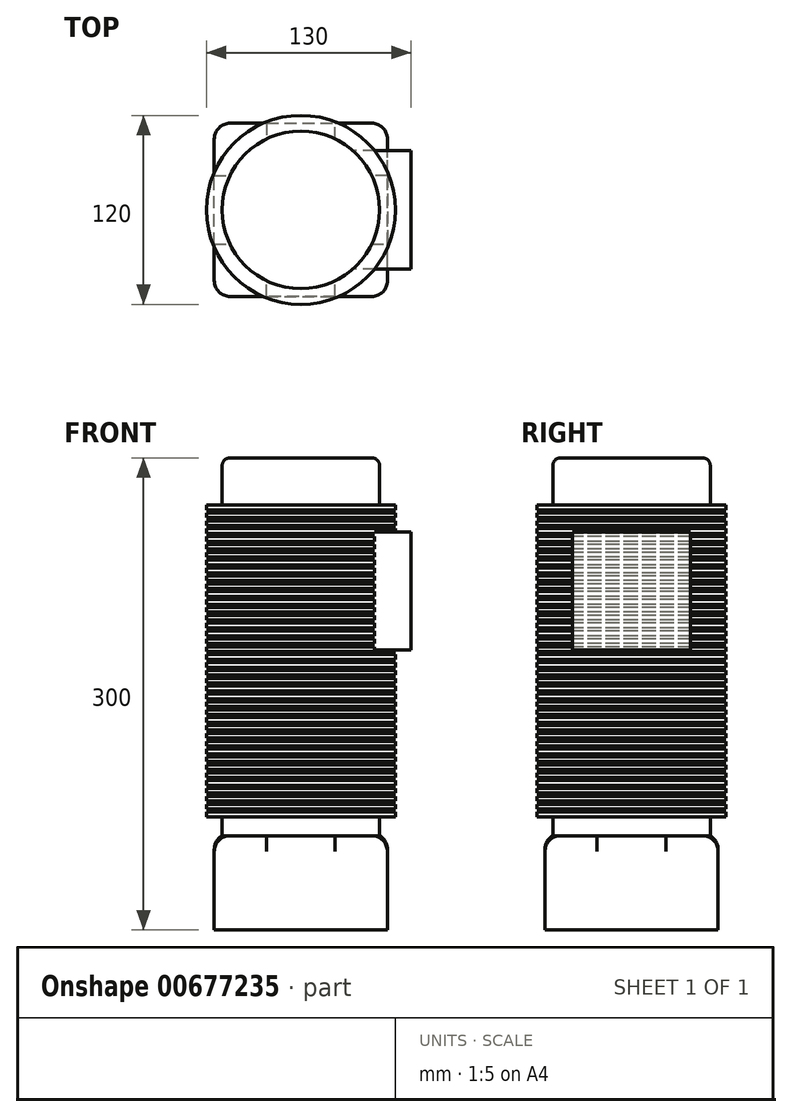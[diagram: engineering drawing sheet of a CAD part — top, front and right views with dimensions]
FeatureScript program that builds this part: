
annotation { "Feature Type Name" : "Feature", "Feature Type Description" : "" }
export const myFeature = defineFeature(function(context is Context, id is Id, definition is map)
    precondition{}
    {
        {
            var Q0;
            Q0=qCreatedBy(makeId("Front.planeOp"),FACE);
            var sketch = newSketch(context, id + "F0", { "sketchPlane" : qUnion([Q0])});
            skLineSegment(sketch, "E0.bottom", {"start": v(0, 0) * mm, "end": v(50, 0) * mm});
            skLineSegment(sketch, "E0.top", {"start": v(0, 300) * mm, "end": v(50, 300) * mm});
            skLineSegment(sketch, "E0.left", {"start": v(0, 0) * mm, "end": v(0, 300) * mm});
            skLineSegment(sketch, "E0.right", {"start": v(50, 0) * mm, "end": v(50, 300) * mm});
            skSolve(sketch);
        }
        {
            var Q0;
            Q0=makeQuery(id+"F0.imprint","IMPRINT",FACE,{"disambiguationData":[TD([[makeQuery(id+"F0.imprint","IMPRINT",EDGE,{"derivedFrom":sQuery(id+"F0.wireOp",EDGE,"E0.bottom")}),1.0]])]});
            var Q1;
            Q1=sQuery(id+"F0.wireOp",EDGE,"E0.left");
            revolve(context, id + "F1", {"entities" : qUnion([Q0]), "axis" : qUnion([Q1]), "revolveType" : RevolveType.FULL});
        }
        {
            var Q0;
            Q0=qCreatedBy(makeId("Front.planeOp"),FACE);
            var sketch = newSketch(context, id + "F2", { "sketchPlane" : qUnion([Q0])});
            skLineSegment(sketch, "E1", {"start": v(50, 300) * mm, "end": v(50, 0) * mm});
            skLineSegment(sketch, "E2.bottom", {"start": v(50, 270) * mm, "end": v(60, 270) * mm});
            skLineSegment(sketch, "E2.top", {"start": v(50, 267) * mm, "end": v(60, 267) * mm});
            skLineSegment(sketch, "E2.left", {"start": v(50, 270) * mm, "end": v(50, 267) * mm});
            skLineSegment(sketch, "E2.right", {"start": v(60, 270) * mm, "end": v(60, 267) * mm});
            skLineSegment(sketch, "E3.0.1.0", {"start": v(50, 265) * mm, "end": v(60, 265) * mm});
            skLineSegment(sketch, "E3.0.1.1", {"start": v(50, 262) * mm, "end": v(60, 262) * mm});
            skLineSegment(sketch, "E3.0.1.2", {"start": v(50, 265) * mm, "end": v(50, 262) * mm});
            skLineSegment(sketch, "E3.0.1.3", {"start": v(60, 265) * mm, "end": v(60, 262) * mm});
            skLineSegment(sketch, "E3.0.2.0", {"start": v(50, 260) * mm, "end": v(60, 260) * mm});
            skLineSegment(sketch, "E3.0.2.1", {"start": v(50, 257) * mm, "end": v(60, 257) * mm});
            skLineSegment(sketch, "E3.0.2.2", {"start": v(50, 260) * mm, "end": v(50, 257) * mm});
            skLineSegment(sketch, "E3.0.2.3", {"start": v(60, 260) * mm, "end": v(60, 257) * mm});
            skLineSegment(sketch, "E3.0.3.0", {"start": v(50, 255) * mm, "end": v(60, 255) * mm});
            skLineSegment(sketch, "E3.0.3.1", {"start": v(50, 252) * mm, "end": v(60, 252) * mm});
            skLineSegment(sketch, "E3.0.3.2", {"start": v(50, 255) * mm, "end": v(50, 252) * mm});
            skLineSegment(sketch, "E3.0.3.3", {"start": v(60, 255) * mm, "end": v(60, 252) * mm});
            skLineSegment(sketch, "E3.0.4.0", {"start": v(50, 250) * mm, "end": v(60, 250) * mm});
            skLineSegment(sketch, "E3.0.4.1", {"start": v(50, 247) * mm, "end": v(60, 247) * mm});
            skLineSegment(sketch, "E3.0.4.2", {"start": v(50, 250) * mm, "end": v(50, 247) * mm});
            skLineSegment(sketch, "E3.0.4.3", {"start": v(60, 250) * mm, "end": v(60, 247) * mm});
            skLineSegment(sketch, "E3.0.5.0", {"start": v(50, 245) * mm, "end": v(60, 245) * mm});
            skLineSegment(sketch, "E3.0.5.1", {"start": v(50, 242) * mm, "end": v(60, 242) * mm});
            skLineSegment(sketch, "E3.0.5.2", {"start": v(50, 245) * mm, "end": v(50, 242) * mm});
            skLineSegment(sketch, "E3.0.5.3", {"start": v(60, 245) * mm, "end": v(60, 242) * mm});
            skLineSegment(sketch, "E3.0.6.0", {"start": v(50, 240) * mm, "end": v(60, 240) * mm});
            skLineSegment(sketch, "E3.0.6.1", {"start": v(50, 237) * mm, "end": v(60, 237) * mm});
            skLineSegment(sketch, "E3.0.6.2", {"start": v(50, 240) * mm, "end": v(50, 237) * mm});
            skLineSegment(sketch, "E3.0.6.3", {"start": v(60, 240) * mm, "end": v(60, 237) * mm});
            skLineSegment(sketch, "E3.0.7.0", {"start": v(50, 235) * mm, "end": v(60, 235) * mm});
            skLineSegment(sketch, "E3.0.7.1", {"start": v(50, 232) * mm, "end": v(60, 232) * mm});
            skLineSegment(sketch, "E3.0.7.2", {"start": v(50, 235) * mm, "end": v(50, 232) * mm});
            skLineSegment(sketch, "E3.0.7.3", {"start": v(60, 235) * mm, "end": v(60, 232) * mm});
            skLineSegment(sketch, "E3.0.8.0", {"start": v(50, 230) * mm, "end": v(60, 230) * mm});
            skLineSegment(sketch, "E3.0.8.1", {"start": v(50, 227) * mm, "end": v(60, 227) * mm});
            skLineSegment(sketch, "E3.0.8.2", {"start": v(50, 230) * mm, "end": v(50, 227) * mm});
            skLineSegment(sketch, "E3.0.8.3", {"start": v(60, 230) * mm, "end": v(60, 227) * mm});
            skLineSegment(sketch, "E3.0.9.0", {"start": v(50, 225) * mm, "end": v(60, 225) * mm});
            skLineSegment(sketch, "E3.0.9.1", {"start": v(50, 222) * mm, "end": v(60, 222) * mm});
            skLineSegment(sketch, "E3.0.9.2", {"start": v(50, 225) * mm, "end": v(50, 222) * mm});
            skLineSegment(sketch, "E3.0.9.3", {"start": v(60, 225) * mm, "end": v(60, 222) * mm});
            skLineSegment(sketch, "E3.0.10.0", {"start": v(50, 220) * mm, "end": v(60, 220) * mm});
            skLineSegment(sketch, "E3.0.10.1", {"start": v(50, 217) * mm, "end": v(60, 217) * mm});
            skLineSegment(sketch, "E3.0.10.2", {"start": v(50, 220) * mm, "end": v(50, 217) * mm});
            skLineSegment(sketch, "E3.0.10.3", {"start": v(60, 220) * mm, "end": v(60, 217) * mm});
            skLineSegment(sketch, "E3.0.11.0", {"start": v(50, 215) * mm, "end": v(60, 215) * mm});
            skLineSegment(sketch, "E3.0.11.1", {"start": v(50, 212) * mm, "end": v(60, 212) * mm});
            skLineSegment(sketch, "E3.0.11.2", {"start": v(50, 215) * mm, "end": v(50, 212) * mm});
            skLineSegment(sketch, "E3.0.11.3", {"start": v(60, 215) * mm, "end": v(60, 212) * mm});
            skLineSegment(sketch, "E3.0.12.0", {"start": v(50, 210) * mm, "end": v(60, 210) * mm});
            skLineSegment(sketch, "E3.0.12.1", {"start": v(50, 207) * mm, "end": v(60, 207) * mm});
            skLineSegment(sketch, "E3.0.12.2", {"start": v(50, 210) * mm, "end": v(50, 207) * mm});
            skLineSegment(sketch, "E3.0.12.3", {"start": v(60, 210) * mm, "end": v(60, 207) * mm});
            skLineSegment(sketch, "E3.0.13.0", {"start": v(50, 205) * mm, "end": v(60, 205) * mm});
            skLineSegment(sketch, "E3.0.13.1", {"start": v(50, 202) * mm, "end": v(60, 202) * mm});
            skLineSegment(sketch, "E3.0.13.2", {"start": v(50, 205) * mm, "end": v(50, 202) * mm});
            skLineSegment(sketch, "E3.0.13.3", {"start": v(60, 205) * mm, "end": v(60, 202) * mm});
            skLineSegment(sketch, "E3.0.14.0", {"start": v(50, 200) * mm, "end": v(60, 200) * mm});
            skLineSegment(sketch, "E3.0.14.1", {"start": v(50, 197) * mm, "end": v(60, 197) * mm});
            skLineSegment(sketch, "E3.0.14.2", {"start": v(50, 200) * mm, "end": v(50, 197) * mm});
            skLineSegment(sketch, "E3.0.14.3", {"start": v(60, 200) * mm, "end": v(60, 197) * mm});
            skLineSegment(sketch, "E3.0.15.0", {"start": v(50, 195) * mm, "end": v(60, 195) * mm});
            skLineSegment(sketch, "E3.0.15.1", {"start": v(50, 192) * mm, "end": v(60, 192) * mm});
            skLineSegment(sketch, "E3.0.15.2", {"start": v(50, 195) * mm, "end": v(50, 192) * mm});
            skLineSegment(sketch, "E3.0.15.3", {"start": v(60, 195) * mm, "end": v(60, 192) * mm});
            skLineSegment(sketch, "E3.0.16.0", {"start": v(50, 190) * mm, "end": v(60, 190) * mm});
            skLineSegment(sketch, "E3.0.16.1", {"start": v(50, 187) * mm, "end": v(60, 187) * mm});
            skLineSegment(sketch, "E3.0.16.2", {"start": v(50, 190) * mm, "end": v(50, 187) * mm});
            skLineSegment(sketch, "E3.0.16.3", {"start": v(60, 190) * mm, "end": v(60, 187) * mm});
            skLineSegment(sketch, "E3.0.17.0", {"start": v(50, 185) * mm, "end": v(60, 185) * mm});
            skLineSegment(sketch, "E3.0.17.1", {"start": v(50, 182) * mm, "end": v(60, 182) * mm});
            skLineSegment(sketch, "E3.0.17.2", {"start": v(50, 185) * mm, "end": v(50, 182) * mm});
            skLineSegment(sketch, "E3.0.17.3", {"start": v(60, 185) * mm, "end": v(60, 182) * mm});
            skLineSegment(sketch, "E3.0.18.0", {"start": v(50, 180) * mm, "end": v(60, 180) * mm});
            skLineSegment(sketch, "E3.0.18.1", {"start": v(50, 177) * mm, "end": v(60, 177) * mm});
            skLineSegment(sketch, "E3.0.18.2", {"start": v(50, 180) * mm, "end": v(50, 177) * mm});
            skLineSegment(sketch, "E3.0.18.3", {"start": v(60, 180) * mm, "end": v(60, 177) * mm});
            skLineSegment(sketch, "E3.0.19.0", {"start": v(50, 175) * mm, "end": v(60, 175) * mm});
            skLineSegment(sketch, "E3.0.19.1", {"start": v(50, 172) * mm, "end": v(60, 172) * mm});
            skLineSegment(sketch, "E3.0.19.2", {"start": v(50, 175) * mm, "end": v(50, 172) * mm});
            skLineSegment(sketch, "E3.0.19.3", {"start": v(60, 175) * mm, "end": v(60, 172) * mm});
            skLineSegment(sketch, "E3.0.20.0", {"start": v(50, 170) * mm, "end": v(60, 170) * mm});
            skLineSegment(sketch, "E3.0.20.1", {"start": v(50, 167) * mm, "end": v(60, 167) * mm});
            skLineSegment(sketch, "E3.0.20.2", {"start": v(50, 170) * mm, "end": v(50, 167) * mm});
            skLineSegment(sketch, "E3.0.20.3", {"start": v(60, 170) * mm, "end": v(60, 167) * mm});
            skLineSegment(sketch, "E3.0.21.0", {"start": v(50, 165) * mm, "end": v(60, 165) * mm});
            skLineSegment(sketch, "E3.0.21.1", {"start": v(50, 162) * mm, "end": v(60, 162) * mm});
            skLineSegment(sketch, "E3.0.21.2", {"start": v(50, 165) * mm, "end": v(50, 162) * mm});
            skLineSegment(sketch, "E3.0.21.3", {"start": v(60, 165) * mm, "end": v(60, 162) * mm});
            skLineSegment(sketch, "E3.0.22.0", {"start": v(50, 160) * mm, "end": v(60, 160) * mm});
            skLineSegment(sketch, "E3.0.22.1", {"start": v(50, 157) * mm, "end": v(60, 157) * mm});
            skLineSegment(sketch, "E3.0.22.2", {"start": v(50, 160) * mm, "end": v(50, 157) * mm});
            skLineSegment(sketch, "E3.0.22.3", {"start": v(60, 160) * mm, "end": v(60, 157) * mm});
            skLineSegment(sketch, "E3.0.23.0", {"start": v(50, 155) * mm, "end": v(60, 155) * mm});
            skLineSegment(sketch, "E3.0.23.1", {"start": v(50, 152) * mm, "end": v(60, 152) * mm});
            skLineSegment(sketch, "E3.0.23.2", {"start": v(50, 155) * mm, "end": v(50, 152) * mm});
            skLineSegment(sketch, "E3.0.23.3", {"start": v(60, 155) * mm, "end": v(60, 152) * mm});
            skLineSegment(sketch, "E3.0.24.0", {"start": v(50, 150) * mm, "end": v(60, 150) * mm});
            skLineSegment(sketch, "E3.0.24.1", {"start": v(50, 147) * mm, "end": v(60, 147) * mm});
            skLineSegment(sketch, "E3.0.24.2", {"start": v(50, 150) * mm, "end": v(50, 147) * mm});
            skLineSegment(sketch, "E3.0.24.3", {"start": v(60, 150) * mm, "end": v(60, 147) * mm});
            skLineSegment(sketch, "E3.0.25.0", {"start": v(50, 145) * mm, "end": v(60, 145) * mm});
            skLineSegment(sketch, "E3.0.25.1", {"start": v(50, 142) * mm, "end": v(60, 142) * mm});
            skLineSegment(sketch, "E3.0.25.2", {"start": v(50, 145) * mm, "end": v(50, 142) * mm});
            skLineSegment(sketch, "E3.0.25.3", {"start": v(60, 145) * mm, "end": v(60, 142) * mm});
            skLineSegment(sketch, "E3.0.26.0", {"start": v(50, 140) * mm, "end": v(60, 140) * mm});
            skLineSegment(sketch, "E3.0.26.1", {"start": v(50, 137) * mm, "end": v(60, 137) * mm});
            skLineSegment(sketch, "E3.0.26.2", {"start": v(50, 140) * mm, "end": v(50, 137) * mm});
            skLineSegment(sketch, "E3.0.26.3", {"start": v(60, 140) * mm, "end": v(60, 137) * mm});
            skLineSegment(sketch, "E3.0.27.0", {"start": v(50, 135) * mm, "end": v(60, 135) * mm});
            skLineSegment(sketch, "E3.0.27.1", {"start": v(50, 132) * mm, "end": v(60, 132) * mm});
            skLineSegment(sketch, "E3.0.27.2", {"start": v(50, 135) * mm, "end": v(50, 132) * mm});
            skLineSegment(sketch, "E3.0.27.3", {"start": v(60, 135) * mm, "end": v(60, 132) * mm});
            skLineSegment(sketch, "E3.0.28.0", {"start": v(50, 130) * mm, "end": v(60, 130) * mm});
            skLineSegment(sketch, "E3.0.28.1", {"start": v(50, 127) * mm, "end": v(60, 127) * mm});
            skLineSegment(sketch, "E3.0.28.2", {"start": v(50, 130) * mm, "end": v(50, 127) * mm});
            skLineSegment(sketch, "E3.0.28.3", {"start": v(60, 130) * mm, "end": v(60, 127) * mm});
            skLineSegment(sketch, "E3.0.29.0", {"start": v(50, 125) * mm, "end": v(60, 125) * mm});
            skLineSegment(sketch, "E3.0.29.1", {"start": v(50, 122) * mm, "end": v(60, 122) * mm});
            skLineSegment(sketch, "E3.0.29.2", {"start": v(50, 125) * mm, "end": v(50, 122) * mm});
            skLineSegment(sketch, "E3.0.29.3", {"start": v(60, 125) * mm, "end": v(60, 122) * mm});
            skLineSegment(sketch, "E3.0.30.0", {"start": v(50, 120) * mm, "end": v(60, 120) * mm});
            skLineSegment(sketch, "E3.0.30.1", {"start": v(50, 117) * mm, "end": v(60, 117) * mm});
            skLineSegment(sketch, "E3.0.30.2", {"start": v(50, 120) * mm, "end": v(50, 117) * mm});
            skLineSegment(sketch, "E3.0.30.3", {"start": v(60, 120) * mm, "end": v(60, 117) * mm});
            skLineSegment(sketch, "E3.0.31.0", {"start": v(50, 115) * mm, "end": v(60, 115) * mm});
            skLineSegment(sketch, "E3.0.31.1", {"start": v(50, 112) * mm, "end": v(60, 112) * mm});
            skLineSegment(sketch, "E3.0.31.2", {"start": v(50, 115) * mm, "end": v(50, 112) * mm});
            skLineSegment(sketch, "E3.0.31.3", {"start": v(60, 115) * mm, "end": v(60, 112) * mm});
            skLineSegment(sketch, "E3.0.32.0", {"start": v(50, 110) * mm, "end": v(60, 110) * mm});
            skLineSegment(sketch, "E3.0.32.1", {"start": v(50, 107) * mm, "end": v(60, 107) * mm});
            skLineSegment(sketch, "E3.0.32.2", {"start": v(50, 110) * mm, "end": v(50, 107) * mm});
            skLineSegment(sketch, "E3.0.32.3", {"start": v(60, 110) * mm, "end": v(60, 107) * mm});
            skLineSegment(sketch, "E3.0.33.0", {"start": v(50, 105) * mm, "end": v(60, 105) * mm});
            skLineSegment(sketch, "E3.0.33.1", {"start": v(50, 102) * mm, "end": v(60, 102) * mm});
            skLineSegment(sketch, "E3.0.33.2", {"start": v(50, 105) * mm, "end": v(50, 102) * mm});
            skLineSegment(sketch, "E3.0.33.3", {"start": v(60, 105) * mm, "end": v(60, 102) * mm});
            skLineSegment(sketch, "E3.0.34.0", {"start": v(50, 100) * mm, "end": v(60, 100) * mm});
            skLineSegment(sketch, "E3.0.34.1", {"start": v(50, 97) * mm, "end": v(60, 97) * mm});
            skLineSegment(sketch, "E3.0.34.2", {"start": v(50, 100) * mm, "end": v(50, 97) * mm});
            skLineSegment(sketch, "E3.0.34.3", {"start": v(60, 100) * mm, "end": v(60, 97) * mm});
            skLineSegment(sketch, "E3.0.35.0", {"start": v(50, 95) * mm, "end": v(60, 95) * mm});
            skLineSegment(sketch, "E3.0.35.1", {"start": v(50, 92) * mm, "end": v(60, 92) * mm});
            skLineSegment(sketch, "E3.0.35.2", {"start": v(50, 95) * mm, "end": v(50, 92) * mm});
            skLineSegment(sketch, "E3.0.35.3", {"start": v(60, 95) * mm, "end": v(60, 92) * mm});
            skLineSegment(sketch, "E3.0.36.0", {"start": v(50, 90) * mm, "end": v(60, 90) * mm});
            skLineSegment(sketch, "E3.0.36.1", {"start": v(50, 87) * mm, "end": v(60, 87) * mm});
            skLineSegment(sketch, "E3.0.36.2", {"start": v(50, 90) * mm, "end": v(50, 87) * mm});
            skLineSegment(sketch, "E3.0.36.3", {"start": v(60, 90) * mm, "end": v(60, 87) * mm});
            skLineSegment(sketch, "E3.0.37.0", {"start": v(50, 85) * mm, "end": v(60, 85) * mm});
            skLineSegment(sketch, "E3.0.37.1", {"start": v(50, 82) * mm, "end": v(60, 82) * mm});
            skLineSegment(sketch, "E3.0.37.2", {"start": v(50, 85) * mm, "end": v(50, 82) * mm});
            skLineSegment(sketch, "E3.0.37.3", {"start": v(60, 85) * mm, "end": v(60, 82) * mm});
            skLineSegment(sketch, "E3.0.38.0", {"start": v(50, 80) * mm, "end": v(60, 80) * mm});
            skLineSegment(sketch, "E3.0.38.1", {"start": v(50, 77) * mm, "end": v(60, 77) * mm});
            skLineSegment(sketch, "E3.0.38.2", {"start": v(50, 80) * mm, "end": v(50, 77) * mm});
            skLineSegment(sketch, "E3.0.38.3", {"start": v(60, 80) * mm, "end": v(60, 77) * mm});
            skLineSegment(sketch, "E3.0.39.0", {"start": v(50, 75) * mm, "end": v(60, 75) * mm});
            skLineSegment(sketch, "E3.0.39.1", {"start": v(50, 72) * mm, "end": v(60, 72) * mm});
            skLineSegment(sketch, "E3.0.39.2", {"start": v(50, 75) * mm, "end": v(50, 72) * mm});
            skLineSegment(sketch, "E3.0.39.3", {"start": v(60, 75) * mm, "end": v(60, 72) * mm});
            skLineSegment(sketch, "E3.direction1", {"start": v(50, 267) * mm, "end": v(75, 267) * mm, "construction": true});
            skLineSegment(sketch, "E3.direction2", {"start": v(50, 267) * mm, "end": v(50, 262) * mm, "construction": true});
            skSolve(sketch);
        }
        {
            var Q0;
            Q0 = qSketchRegion(id + "F2", true);
            var Q1;
            Q1=makeQuery(id+"F1.opRevolve","SWEPT_FACE",FACE,{"disambiguationData":[OSD([sQuery(id+"F0.wireOp",EDGE,"E0.right")])]});
            revolve(context, id + "F3", {"operationType" : NewBodyOperationType.ADD, "entities" : qUnion([Q0]), "axis" : qUnion([Q1]), "revolveType" : RevolveType.FULL});
        }
        {
            var Q0;
            Q0=makeQuery(id+"F1.opRevolve","SWEPT_EDGE",EDGE,{"disambiguationData":[OSD([sQuery(id+"F0.wireOp",EDGE,"E0.top"),sQuery(id+"F0.wireOp",EDGE,"E0.right")])]});
            fillet(context, id + "F4", {"entities" : qUnion([Q0]), "radius" : 5 * mm, "tangentPropagation" : true, "allowEdgeOverflow" : false});
        }
        {
            var Q0;
            Q0=qCreatedBy(makeId("Top.planeOp"),FACE);
            var sketch = newSketch(context, id + "F5", { "sketchPlane" : qUnion([Q0])});
            skLineSegment(sketch, "E4.bottom", {"start": v(-55, -55) * mm, "end": v(55, -55) * mm});
            skLineSegment(sketch, "E4.top", {"start": v(-55, 55) * mm, "end": v(55, 55) * mm});
            skLineSegment(sketch, "E4.left", {"start": v(-55, -55) * mm, "end": v(-55, 55) * mm});
            skLineSegment(sketch, "E4.right", {"start": v(55, -55) * mm, "end": v(55, 55) * mm});
            skPoint(sketch, "E4.middle", {"position": v(0, 0) * mm});
            skSolve(sketch);
        }
        {
            var Q0;
            Q0=makeQuery(id+"F5.imprint","IMPRINT",FACE,{"disambiguationData":[TD([[makeQuery(id+"F5.imprint","IMPRINT",EDGE,{"derivedFrom":sQuery(id+"F5.wireOp",EDGE,"E4.bottom")}),1.0]])]});
            extrude(context, id + "F6", {"entities" : qUnion([Q0]), "operationType" : NewBodyOperationType.ADD, "depth" : 60 * mm, "offsetDistance" : 25 * mm});
        }
        {
            var Q0;
            Q0=makeQuery(id+"F6.opExtrude","SWEPT_EDGE",EDGE,{"disambiguationData":[OSD([sQuery(id+"F5.wireOp",EDGE,"E4.bottom"),sQuery(id+"F5.wireOp",EDGE,"E4.left")])]});
            var Q1;
            Q1=makeQuery(id+"F6.opExtrude","CAP_EDGE",EDGE,{"disambiguationData":[OSD([sQuery(id+"F5.wireOp",EDGE,"E4.bottom")])],"isStart":false});
            var Q2;
            Q2=makeQuery(id+"F6.opExtrude","CAP_EDGE",EDGE,{"disambiguationData":[OSD([sQuery(id+"F5.wireOp",EDGE,"E4.left")])],"isStart":false});
            var Q3;
            Q3=makeQuery(id+"F6.opExtrude","SWEPT_EDGE",EDGE,{"disambiguationData":[OSD([sQuery(id+"F5.wireOp",EDGE,"E4.bottom"),sQuery(id+"F5.wireOp",EDGE,"E4.right")])]});
            var Q4;
            Q4=makeQuery(id+"F6.opExtrude","CAP_EDGE",EDGE,{"disambiguationData":[OSD([sQuery(id+"F5.wireOp",EDGE,"E4.right")])],"isStart":false});
            var Q5;
            Q5=makeQuery(id+"F6.opExtrude","SWEPT_EDGE",EDGE,{"disambiguationData":[OSD([sQuery(id+"F5.wireOp",EDGE,"E4.top"),sQuery(id+"F5.wireOp",EDGE,"E4.right")])]});
            var Q6;
            Q6=makeQuery(id+"F6.opExtrude","CAP_EDGE",EDGE,{"disambiguationData":[OSD([sQuery(id+"F5.wireOp",EDGE,"E4.top")])],"isStart":false});
            var Q7;
            Q7=makeQuery(id+"F6.opExtrude","SWEPT_EDGE",EDGE,{"disambiguationData":[OSD([sQuery(id+"F5.wireOp",EDGE,"E4.top"),sQuery(id+"F5.wireOp",EDGE,"E4.left")])]});
            fillet(context, id + "F7", {"entities" : qUnion([Q0, Q1, Q2, Q3, Q4, Q5, Q6, Q7]), "radius" : 10 * mm, "tangentPropagation" : true, "allowEdgeOverflow" : false});
        }
        {
            var Q0;
            Q0=makeQuery(id+"F6.opExtrude","SWEPT_FACE",FACE,{"disambiguationData":[OSD([sQuery(id+"F5.wireOp",EDGE,"E4.right")])]});
            var sketch = newSketch(context, id + "F8", { "sketchPlane" : qUnion([Q0])});
            skLineSegment(sketch, "E5.bottom", {"start": v(37.5, 177.94) * mm, "end": v(-37.5, 177.94) * mm});
            skLineSegment(sketch, "E5.top", {"start": v(37.5, 252.94) * mm, "end": v(-37.5, 252.94) * mm});
            skLineSegment(sketch, "E5.left", {"start": v(37.5, 177.94) * mm, "end": v(37.5, 252.94) * mm});
            skLineSegment(sketch, "E5.right", {"start": v(-37.5, 177.94) * mm, "end": v(-37.5, 252.94) * mm});
            skPoint(sketch, "E5.middle", {"position": v(0, 215.44) * mm});
            skSolve(sketch);
        }
        {
            var Q0;
            Q0 = qSketchRegion(id + "F8", true);
            extrude(context, id + "F9", {"entities" : qUnion([Q0]), "operationType" : NewBodyOperationType.ADD, "oppositeDirection" : true, "depth" : 25 * mm, "offsetDistance" : 25 * mm, "hasSecondDirection" : true, "secondDirectionOppositeDirection" : false, "secondDirectionDepth" : 15 * mm});
        }
    });
